# Revit family: ECOJET-15DIA-LENGTH
name_source: partatom
category: Air Terminals
revit_build: Autodesk Revit 2018 (Build: 20170223_1515(x64)
units: mm (PartAtom-declared; Revit-internal decimal feet)

## family parameters
Always vertical = Yes
Cut with Voids When Loaded = No
Part Type = Normal
Room Calculation Point = No
Round Connector Dimension = Use Diameter
Shared = No
Work Plane-Based = No

## types (8) — shared parameters
ADIM = 0' - 5"
BOXHI = 1' - 4"
FRONTOPENDING = 0' - 9 3/4"
HIOVER = 0' - 2"
IJOPENING = 1' - 1 7/8"
Manufacturer = ANEMOSTAT-HVAC
Model = ECOJET DRUM LOUVER
NORHI = 1' - 3"
RADIUS = 0' - 7 1/2"
Thickness = 0' - 0 1/16"
URL = anemostat-hvac.com
WIDOVER = 0' - 2 3/4"

## per-type parameters (varying)
| type | BLADE | BOXWID | DUCTWID | INSIDECUT | NORMLENGTH | NORWID |
| ECOJET-15-15D | 2 | 1' - 5 11/16" | 1' - 4" | 1' - 2 3/4" | 1' - 3" | 1' - 2 15/16" |
| ECOJET-20-15D | 3 | 1' - 10 11/16" | 1' - 9" | 1' - 7 3/4" | 1' - 8" | 1' - 7 15/16" |
| ECOJET-25-15D | 4 | 2' - 3 11/16" | 2' - 2" | 2' - 0 3/4" | 2' - 1" | 2' - 0 15/16" |
| ECOJET-30-15D | 5 | 2' - 8 11/16" | 2' - 7" | 2' - 5 3/4" | 2' - 6" | 2' - 5 15/16" |
| ECOJET-40-15D | 7 | 3' - 6 11/16" | 3' - 5" | 3' - 3 3/4" | 3' - 4" | 3' - 3 15/16" |
| ECOJET-50-15D | 9 | 4' - 4 11/16" | 4' - 3" | 4' - 1 3/4" | 4' - 2" | 4' - 1 15/16" |
| ECOJET-60-15D | 11 | 5' - 2 11/16" | 5' - 1" | 4' - 11 3/4" | 5' - 0" | 4' - 11 15/16" |
| ECOJET-70-15D | 13 | 6' - 0 11/16" | 5' - 11" | 5' - 9 3/4" | 5' - 10" | 5' - 9 15/16" |

## geometry (parser evidence)
native form markers: Sweep x14
no freeform markers — native parametric forms only
